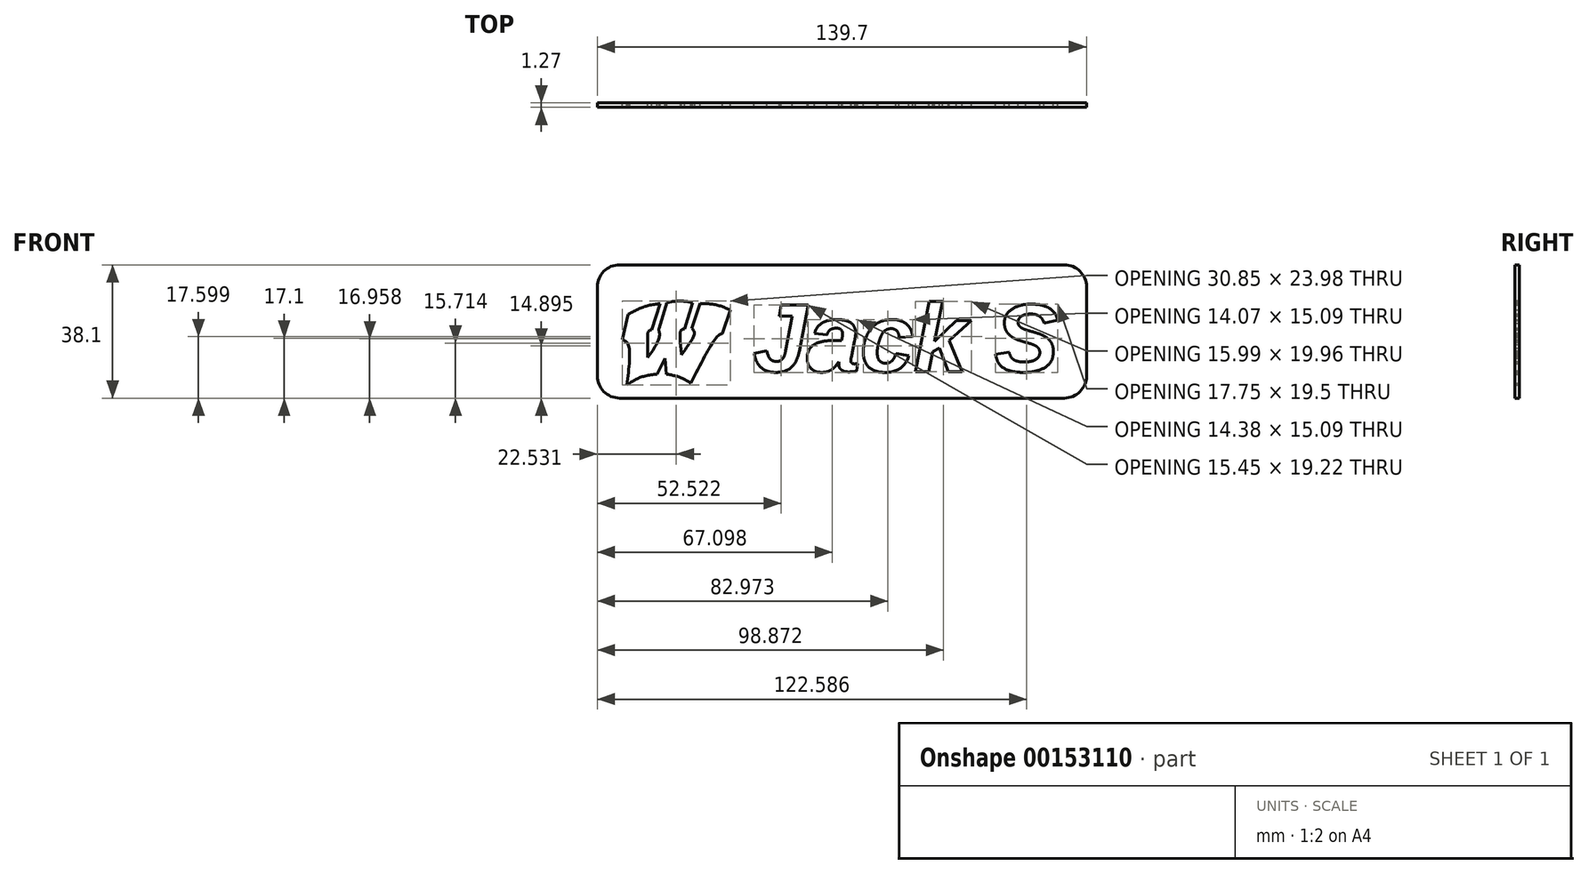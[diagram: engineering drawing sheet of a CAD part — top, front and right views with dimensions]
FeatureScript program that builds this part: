
annotation { "Feature Type Name" : "Feature", "Feature Type Description" : "" }
export const myFeature = defineFeature(function(context is Context, id is Id, definition is map)
    precondition{}
    {
        {
            var Q0;
            Q0=qCreatedBy(makeId("Front.planeOp"),FACE);
            var sketch = newSketch(context, id + "F0", { "sketchPlane" : qUnion([Q0])});
            skFitSpline(sketch, "E0", {"points": [v(52.25, 0.96) * mm, v(53.93, -0.37) * mm, v(53.58, -12.03) * mm], "startDerivative": vector(6.52, -2.6) * mm, "endDerivative": vector(-2.63, -20.93) * mm});
            skFitSpline(sketch, "E1", {"points": [v(53.58, -12.03) * mm, v(57.3, -9.88) * mm, v(62.16, -8.9) * mm], "startDerivative": vector(7.3, 5.07) * mm, "endDerivative": vector(9.83, 1.24) * mm});
            skLineSegment(sketch, "E2", {"start": v(62.16, -8.9) * mm, "end": v(64.42, -4.43) * mm});
            skLineSegment(sketch, "E3", {"start": v(64.42, -4.43) * mm, "end": v(64.83, -8.9) * mm});
            skFitSpline(sketch, "E4", {"points": [v(64.83, -8.9) * mm, v(68.77, -9.82) * mm, v(71.85, -11.5) * mm], "startDerivative": vector(7.93, -1.35) * mm, "endDerivative": vector(6.08, -3.9) * mm});
            skFitSpline(sketch, "E5", {"points": [v(71.85, -11.5) * mm, v(79.5, 1.95) * mm, v(80.9, 2.7) * mm], "startDerivative": vector(11.75, 23.3) * mm, "endDerivative": vector(5.22, 1.34) * mm});
            skLineSegment(sketch, "E6", {"start": v(80.9, 2.7) * mm, "end": v(83.1, 9.43) * mm});
            skFitSpline(sketch, "E7", {"points": [v(83.1, 9.43) * mm, v(79.15, 10.87) * mm, v(74.52, 11.3) * mm], "startDerivative": vector(-7.87, 3.48) * mm, "endDerivative": vector(-9.28, 0.37) * mm});
            skLineSegment(sketch, "E8", {"start": v(74.52, 11.3) * mm, "end": v(72.15, 4.16) * mm});
            skFitSpline(sketch, "E9", {"points": [v(72.15, 4.16) * mm, v(72.76, 3.3) * mm, v(72.67, 2) * mm, v(69.2, -3.3) * mm], "startDerivative": vector(3.3, -3.79) * mm, "endDerivative": vector(-8.37, -11.36) * mm});
            skFitSpline(sketch, "E10", {"points": [v(69.2, -3.3) * mm, v(68.76, 2.73) * mm, v(69.2, 3.73) * mm, v(70.02, 4.03) * mm], "startDerivative": vector(-1.55, 13.06) * mm, "endDerivative": vector(4.32, 1) * mm});
            skLineSegment(sketch, "E11", {"start": v(70.02, 4.03) * mm, "end": v(72.32, 11.5) * mm});
            skFitSpline(sketch, "E12", {"points": [v(72.32, 11.5) * mm, v(69.02, 11.96) * mm, v(64.92, 11.5) * mm], "startDerivative": vector(-6.88, 2.24) * mm, "endDerivative": vector(-7.92, -2.18) * mm});
            skLineSegment(sketch, "E13", {"start": v(64.92, 11.5) * mm, "end": v(62.82, 4.23) * mm});
            skFitSpline(sketch, "E14", {"points": [v(62.82, 4.23) * mm, v(62.82, 3.14) * mm, v(62.82, 1.58) * mm, v(59.58, -4.1) * mm], "startDerivative": vector(-2.24, -7.18) * mm, "endDerivative": vector(-8.41, -11.52) * mm});
            skLineSegment(sketch, "E15", {"start": v(59.58, -4.1) * mm, "end": v(59.58, 2.86) * mm});
            skLineSegment(sketch, "E16", {"start": v(60.63, 3.78) * mm, "end": v(63.02, 11.21) * mm});
            skFitSpline(sketch, "E17", {"points": [v(63.02, 11.21) * mm, v(58.56, 10.4) * mm, v(54, 8.22) * mm], "startDerivative": vector(-9.59, -0.82) * mm, "endDerivative": vector(-8.84, -4.97) * mm});
            skLineSegment(sketch, "E18", {"start": v(54, 8.22) * mm, "end": v(52.25, 0.96) * mm});
            skFitSpline(sketch, "E19", {"points": [v(59.58, 2.86) * mm, v(59.94, 3.51) * mm, v(60.63, 3.78) * mm], "startDerivative": vector(0.55, 1.5) * mm, "endDerivative": vector(1.55, 0.34) * mm});
            skLineSegment(sketch, "E20.bottom", {"start": v(51.5, 22.35) * mm, "end": v(178.5, 22.35) * mm});
            skLineSegment(sketch, "E20.top", {"start": v(51.5, -15.75) * mm, "end": v(178.5, -15.75) * mm});
            skLineSegment(sketch, "E20.left", {"start": v(45.14, 16) * mm, "end": v(45.14, -9.4) * mm});
            skLineSegment(sketch, "E20.right", {"start": v(184.84, 16) * mm, "end": v(184.84, -9.4) * mm});
            skText(sketch, "E21", { "text": "Jack S", "fontName": "Arimo-BoldItalic.ttf"});
            skPoint(sketch, "E22.visualSharp", {"position": v(45.14, 22.35) * mm});
            skArc(sketch, "E22.filletArc", {"start": v(51.5, 22.35) * mm, "mid": v(47, 20.49) * mm, "end": v(45.14, 16) * mm});
            skPoint(sketch, "E23.visualSharp", {"position": v(45.14, -15.75) * mm});
            skArc(sketch, "E23.filletArc", {"start": v(45.14, -9.4) * mm, "mid": v(47, -13.9) * mm, "end": v(51.5, -15.75) * mm});
            skPoint(sketch, "E24.visualSharp", {"position": v(184.84, 22.35) * mm});
            skArc(sketch, "E24.filletArc", {"start": v(184.84, 16) * mm, "mid": v(182.98, 20.49) * mm, "end": v(178.5, 22.35) * mm});
            skPoint(sketch, "E25.visualSharp", {"position": v(184.84, -15.75) * mm});
            skArc(sketch, "E25.filletArc", {"start": v(178.5, -15.75) * mm, "mid": v(182.98, -13.9) * mm, "end": v(184.84, -9.4) * mm});
            const initialGuessF0  = {"E21": [0.0896, -0.00813, 1, 0, 0.01983]};
            skSetInitialGuess(sketch, initialGuessF0);
            skSolve(sketch);
        }
        {
            var Q0;
            Q0=makeQuery(id+"F0.imprint","IMPRINT",FACE,{"disambiguationData":[TD([[makeQuery(id+"F0.imprint","IMPRINT",EDGE,{"derivedFrom":sQuery(id+"F0.wireOp",EDGE,"E0")}),-1.0]])]});
            extrude(context, id + "F1", {"entities" : qUnion([Q0]), "depth" : 1.27 * mm});
        }
    });
